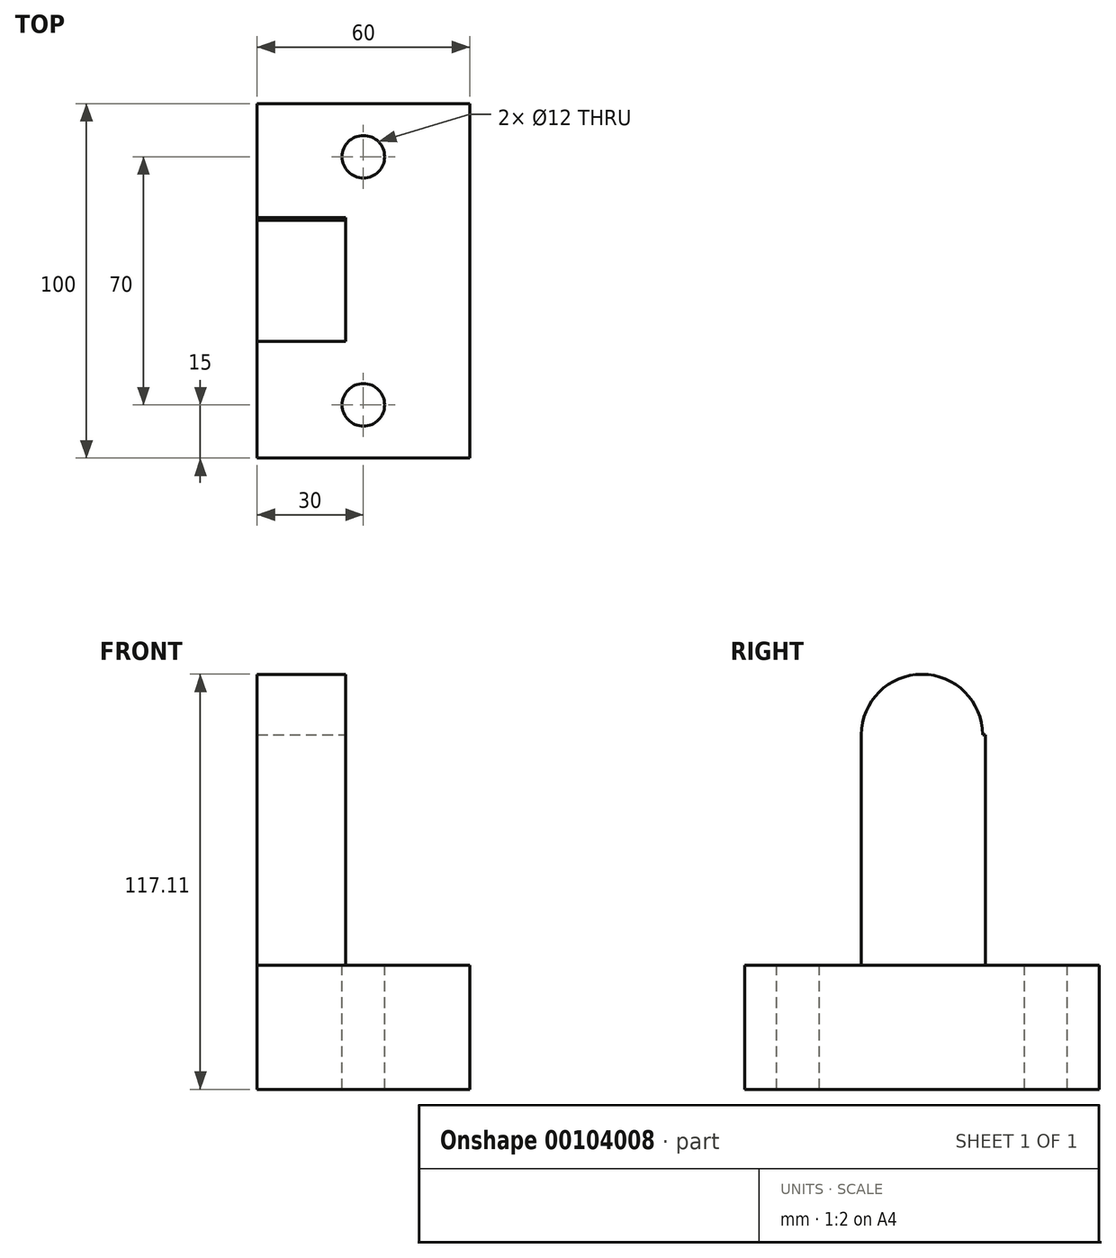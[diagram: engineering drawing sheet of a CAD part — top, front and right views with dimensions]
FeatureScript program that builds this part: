
annotation { "Feature Type Name" : "Feature", "Feature Type Description" : "" }
export const myFeature = defineFeature(function(context is Context, id is Id, definition is map)
    precondition{}
    {
        {
            var Q0;
            Q0=qCreatedBy(makeId("Top.planeOp"),FACE);
            var sketch = newSketch(context, id + "F0", { "sketchPlane" : qUnion([Q0])});
            skLineSegment(sketch, "E0.bottom", {"start": v(30, -50) * mm, "end": v(-30, -50) * mm});
            skLineSegment(sketch, "E0.top", {"start": v(30, 50) * mm, "end": v(-30, 50) * mm});
            skLineSegment(sketch, "E0.left", {"start": v(30, -50) * mm, "end": v(30, 50) * mm});
            skLineSegment(sketch, "E0.right", {"start": v(-30, -50) * mm, "end": v(-30, 50) * mm});
            skPoint(sketch, "E0.middle", {"position": v(0, 0) * mm});
            skSolve(sketch);
        }
        {
            var Q0;
            Q0=makeQuery(id+"F0.imprint","IMPRINT",FACE,{"disambiguationData":[TD([[makeQuery(id+"F0.imprint","IMPRINT",EDGE,{"derivedFrom":sQuery(id+"F0.wireOp",EDGE,"E0.bottom")}),-1.0]])]});
            extrude(context, id + "F1", {"entities" : qUnion([Q0]), "depth" : 100 * mm});
        }
        {
            var Q0;
            Q0=makeQuery(id+"F1.opExtrude","CAP_FACE",FACE,{"disambiguationData":[OSD([sQuery(id+"F0.wireOp",EDGE,"E0.bottom"),sQuery(id+"F0.wireOp",EDGE,"E0.top"),sQuery(id+"F0.wireOp",EDGE,"E0.left"),sQuery(id+"F0.wireOp",EDGE,"E0.right")])],"isStart":false});
            var sketch = newSketch(context, id + "F2", { "sketchPlane" : qUnion([Q0])});
            skCircle(sketch, "E1", {"center": v(0, -35) * mm, "radius": 6 * mm});
            skCircle(sketch, "E2", {"center": v(0, 35) * mm, "radius": 6 * mm});
            skSolve(sketch);
        }
        {
            var Q0;
            Q0=makeQuery(id+"F2.imprint","IMPRINT",FACE,{"disambiguationData":[TD([[makeQuery(id+"F2.imprint","IMPRINT",EDGE,{"derivedFrom":sQuery(id+"F2.wireOp",EDGE,"E2")}),1.0]])]});
            var Q1;
            Q1=makeQuery(id+"F2.imprint","IMPRINT",FACE,{"disambiguationData":[TD([[makeQuery(id+"F2.imprint","IMPRINT",EDGE,{"derivedFrom":sQuery(id+"F2.wireOp",EDGE,"E1")}),1.0]])]});
            extrude(context, id + "F3", {"entities" : qUnion([Q0, Q1]), "operationType" : NewBodyOperationType.REMOVE, "oppositeDirection" : true, "depth" : 100 * mm});
        }
        {
            var Q0;
            Q0=makeQuery(id+"F1.opExtrude","CAP_FACE",FACE,{"disambiguationData":[OSD([sQuery(id+"F0.wireOp",EDGE,"E0.bottom"),sQuery(id+"F0.wireOp",EDGE,"E0.top"),sQuery(id+"F0.wireOp",EDGE,"E0.left"),sQuery(id+"F0.wireOp",EDGE,"E0.right")])],"isStart":false});
            var sketch = newSketch(context, id + "F4", { "sketchPlane" : qUnion([Q0])});
            skLineSegment(sketch, "E3.bottom", {"start": v(-30, 17.9) * mm, "end": v(-5, 17.9) * mm});
            skLineSegment(sketch, "E3.top", {"start": v(-30, -17.1) * mm, "end": v(-5, -17.1) * mm});
            skLineSegment(sketch, "E3.left", {"start": v(-30, 17.9) * mm, "end": v(-30, -17.1) * mm});
            skLineSegment(sketch, "E3.right", {"start": v(-5, 17.9) * mm, "end": v(-5, -17.1) * mm});
            skSolve(sketch);
        }
        {
            var Q0;
            {var subQ2=sQuery(id+"F4.wireOp",EDGE,"E3.bottom");Q0=makeQuery(id+"F4.imprint","IMPRINT",FACE,{"disambiguationData":[TD([[makeQuery(id+"F4.imprint","IMPRINT",EDGE,{"derivedFrom":subQ2}),1.0]])]});}
            extrude(context, id + "F5", {"entities" : qUnion([Q0]), "operationType" : NewBodyOperationType.REMOVE, "oppositeDirection" : true, "depth" : 65 * mm});
        }
        {
            var Q0;
            Q0=makeQuery(id+"F1.opExtrude","CAP_FACE",FACE,{"disambiguationData":[OSD([sQuery(id+"F0.wireOp",EDGE,"E0.bottom"),sQuery(id+"F0.wireOp",EDGE,"E0.top"),sQuery(id+"F0.wireOp",EDGE,"E0.left"),sQuery(id+"F0.wireOp",EDGE,"E0.right")])],"isStart":false});
            var sketch = newSketch(context, id + "F6", { "sketchPlane" : qUnion([Q0])});
            skLineSegment(sketch, "E4", {"start": v(-30, 0) * mm, "end": v(-5, 0) * mm});
            skSolve(sketch);
        }
        {
            var Q0;
            {var subQ0=sQuery(id+"F6.wireOp",EDGE,"E4");Q0=makeQuery(id+"F6.imprint","IMPRINT",FACE,{"disambiguationData":[TD([[makeQuery(id+"F6.imprint","IMPRINT",EDGE,{"derivedFrom":subQ0}),-1.0]])]});}
            var Q1;
            Q1=sQuery(id+"F6.wireOp",EDGE,"E4");
            revolve(context, id + "F7", {"operationType" : NewBodyOperationType.ADD, "entities" : qUnion([Q0]), "axis" : qUnion([Q1]), "revolveType" : RevolveType.ONE_DIRECTION, "oppositeDirection" : true, "angle" : 180 * degree});
        }
    });
